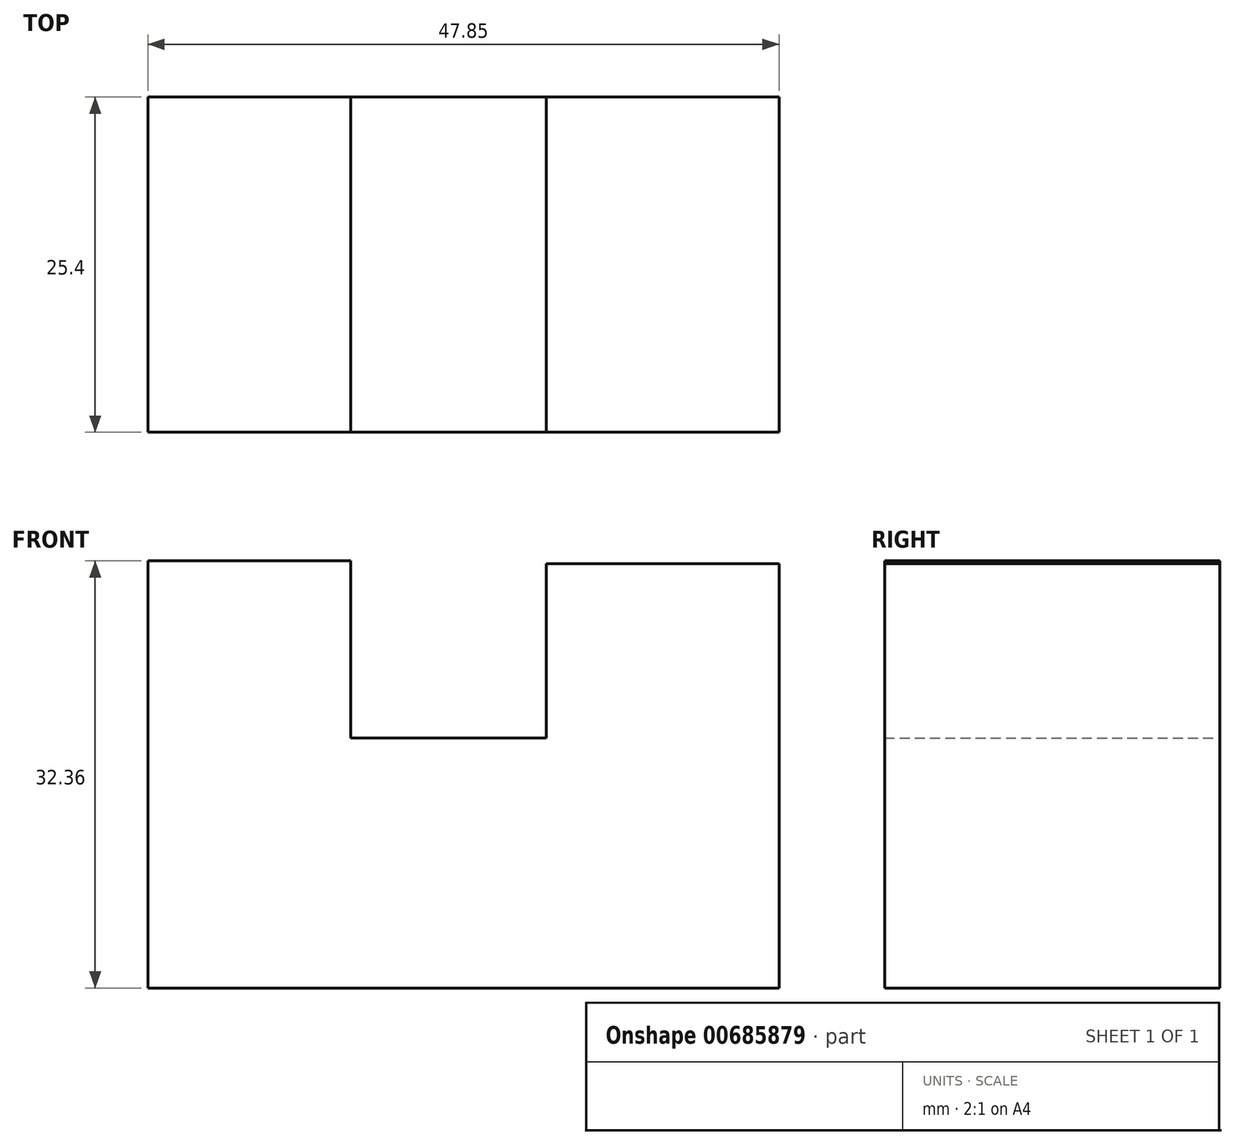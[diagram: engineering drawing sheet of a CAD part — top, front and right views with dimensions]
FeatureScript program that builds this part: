
annotation { "Feature Type Name" : "Feature", "Feature Type Description" : "" }
export const myFeature = defineFeature(function(context is Context, id is Id, definition is map)
    precondition{}
    {
        {
            var Q0;
            Q0=qCreatedBy(makeId("Front.planeOp"),FACE);
            var sketch = newSketch(context, id + "F0", { "sketchPlane" : qUnion([Q0])});
            skLineSegment(sketch, "E0", {"start": v(0, 0) * mm, "end": v(-47.85, 0) * mm});
            skLineSegment(sketch, "E1", {"start": v(-47.85, 0) * mm, "end": v(-47.85, 32.36) * mm});
            skLineSegment(sketch, "E2", {"start": v(-47.85, 32.36) * mm, "end": v(-32.46, 32.36) * mm});
            skLineSegment(sketch, "E3", {"start": v(-32.46, 32.36) * mm, "end": v(-32.46, 18.94) * mm});
            skLineSegment(sketch, "E4", {"start": v(-32.46, 18.94) * mm, "end": v(-17.66, 18.94) * mm});
            skLineSegment(sketch, "E5", {"start": v(-17.66, 18.94) * mm, "end": v(-17.66, 32.16) * mm});
            skLineSegment(sketch, "E6", {"start": v(-17.66, 32.16) * mm, "end": v(0, 32.16) * mm});
            skLineSegment(sketch, "E7", {"start": v(0, 32.16) * mm, "end": v(0, 0) * mm});
            skSolve(sketch);
        }
        {
            var Q0;
            Q0 = qSketchRegion(id + "F0", true);
            extrude(context, id + "F1", {"entities" : qUnion([Q0]), "depth" : 25.4 * mm, "offsetDistance" : 25.4 * mm});
        }
    });
